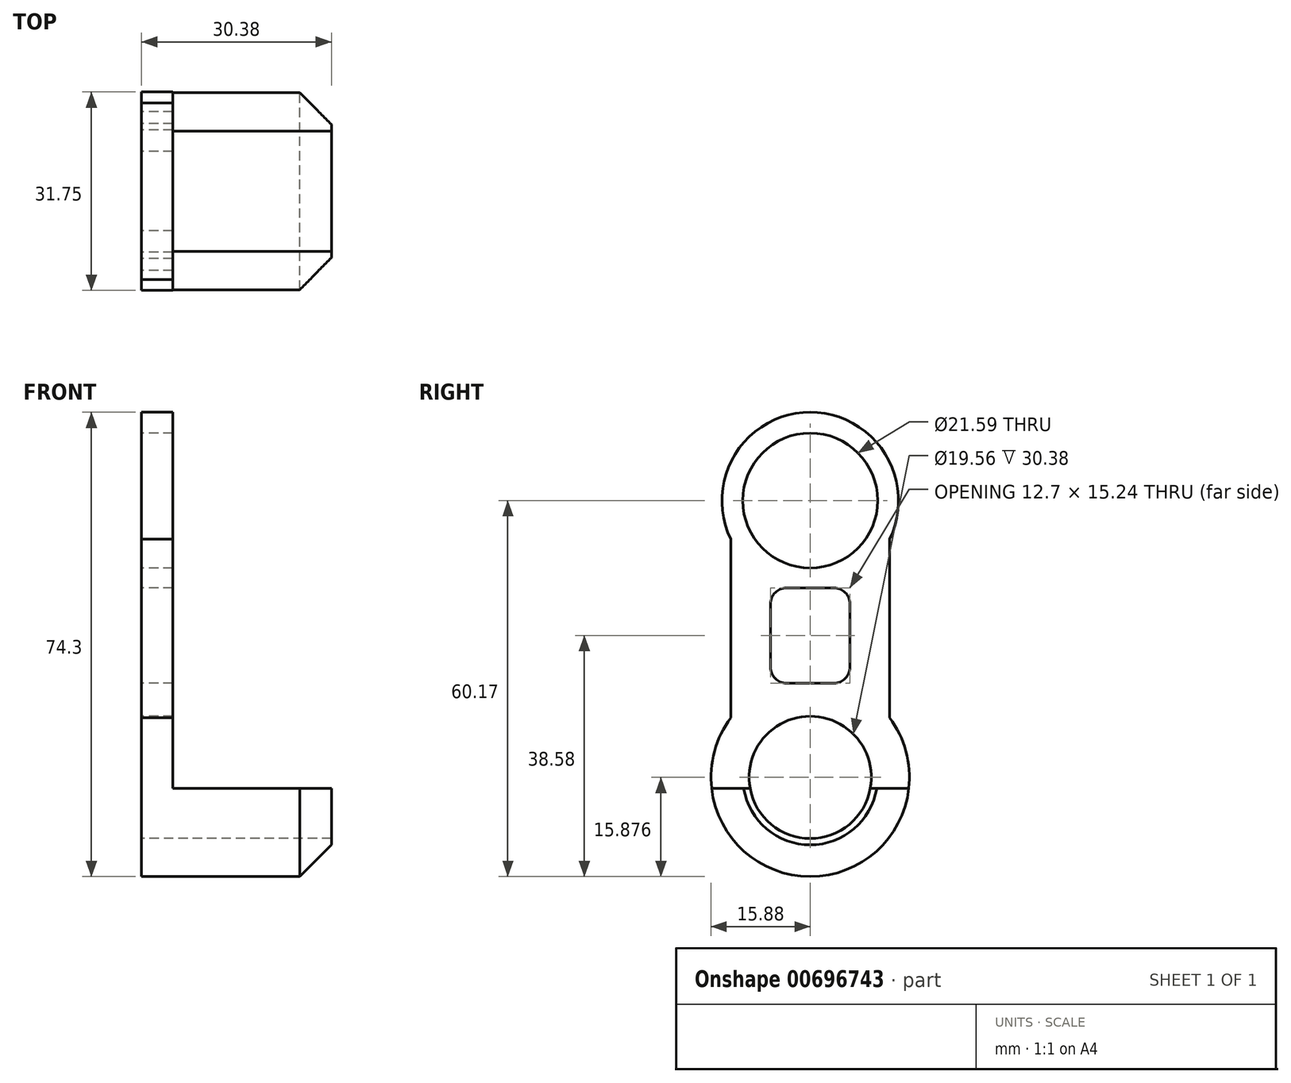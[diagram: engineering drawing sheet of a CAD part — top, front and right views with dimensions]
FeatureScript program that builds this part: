
annotation { "Feature Type Name" : "Feature", "Feature Type Description" : "" }
export const myFeature = defineFeature(function(context is Context, id is Id, definition is map)
    precondition{}
    {
        {
            var Q0;
            Q0=qCreatedBy(makeId("Right.planeOp"),FACE);
            var sketch = newSketch(context, id + "F0", { "sketchPlane" : qUnion([Q0])});
            skCircle(sketch, "E0", {"center": v(0, 0) * mm, "radius": 10.8 * mm});
            skArc(sketch, "E1", {"start": v(12.7, -6.2) * mm, "mid": v(0, 14.13) * mm, "end": v(-12.7, -6.2) * mm});
            skLineSegment(sketch, "E2", {"start": v(-12.7, -6.2) * mm, "end": v(-12.7, -34.77) * mm});
            skLineSegment(sketch, "E3", {"start": v(12.7, -6.2) * mm, "end": v(12.7, -34.77) * mm});
            skCircle(sketch, "E4", {"center": v(0, -44.3) * mm, "radius": 9.78 * mm});
            skArc(sketch, "E5", {"start": v(-12.7, -34.77) * mm, "mid": v(0, -60.17) * mm, "end": v(12.7, -34.77) * mm});
            skLineSegment(sketch, "E6", {"start": v(6.35, -13.97) * mm, "end": v(6.35, -29.21) * mm});
            skLineSegment(sketch, "E7", {"start": v(6.35, -29.21) * mm, "end": v(-6.35, -29.21) * mm});
            skLineSegment(sketch, "E8", {"start": v(-6.35, -29.21) * mm, "end": v(-6.35, -13.97) * mm});
            skLineSegment(sketch, "E9", {"start": v(-6.35, -13.97) * mm, "end": v(6.35, -13.97) * mm});
            skSolve(sketch);
        }
        {
            var Q0;
            Q0=makeQuery(id+"F0.imprint","IMPRINT",FACE,{"disambiguationData":[TD([[makeQuery(id+"F0.imprint","IMPRINT",EDGE,{"derivedFrom":sQuery(id+"F0.wireOp",EDGE,"E0")}),-1.0]])]});
            var Q1;
            {var subQ1=sQuery(id+"F0.wireOp",EDGE,"E2");Q1=makeQuery(id+"F0.imprint","IMPRINT",FACE,{"disambiguationData":[TD([[makeQuery(id+"F0.imprint","IMPRINT",EDGE,{"derivedFrom":subQ1}),1.0]])]});}
            var Q2;
            {var subQ0=sQuery(id+"F0.wireOp",EDGE,"MDCRhlGj-Whgg-Ktwf-GIel-y43xcJZ2J1TR");Q2=makeQuery(id+"F0.imprint","IMPRINT",FACE,{"disambiguationData":[TD([[makeQuery(id+"F0.imprint","IMPRINT",EDGE,{"derivedFrom":subQ0}),-1.0]])]});}
            var Q3;
            Q3=makeQuery(id+"F0.imprint","IMPRINT",FACE,{"disambiguationData":[TD([[makeQuery(id+"F0.imprint","IMPRINT",EDGE,{"derivedFrom":sQuery(id+"F0.wireOp",EDGE,"E4")}),-1.0]])]});
            var Q4;
            {var subQ0=sQuery(id+"F0.wireOp",EDGE,"E5");var subQ1=sQuery(id+"F0.wireOp",EDGE,"5xRPiuOo-jEAR-rATj-yGpN-2LbGpSY4B5gd");var subQ2=makeQuery(id+"F0.imprint","INTERSECT",VERTEX,{"disambiguationData":[OD(0.0)],"derivedFrom":[subQ1,subQ0]});Q4=makeQuery(id+"F0.imprint","IMPRINT",FACE,{"disambiguationData":[TD([[makeQuery(id+"F0.imprint","IMPRINT",EDGE,{"disambiguationData":[TD([[subQ2,-1.0]])],"derivedFrom":subQ1}),1.0]])]});}
            extrude(context, id + "F1", {"entities" : qUnion([Q0, Q1, Q2, Q3, Q4]), "depth" : 4.98 * mm, "offsetDistance" : 25.4 * mm});
        }
        {
            var Q0;
            Q0=makeQuery(id+"F1.opExtrude","CAP_FACE",FACE,{"disambiguationData":[OSD([sQuery(id+"F0.wireOp",EDGE,"E0"),sQuery(id+"F0.wireOp",EDGE,"E1"),sQuery(id+"F0.wireOp",EDGE,"E2"),sQuery(id+"F0.wireOp",EDGE,"E3"),sQuery(id+"F0.wireOp",EDGE,"E4"),sQuery(id+"F0.wireOp",EDGE,"E5")])],"isStart":false});
            var sketch = newSketch(context, id + "F2", { "sketchPlane" : qUnion([Q0])});
            skCircle(sketch, "E10.0", {"center": v(0, -44.3) * mm, "radius": 9.78 * mm});
            skArc(sketch, "E11.0", {"start": v(-12.7, -34.77) * mm, "mid": v(0, -60.17) * mm, "end": v(12.7, -34.77) * mm});
            skLineSegment(sketch, "E12", {"start": v(-9.62, -46.07) * mm, "end": v(-15.78, -46.07) * mm});
            skLineSegment(sketch, "E13", {"start": v(9.62, -46.07) * mm, "end": v(15.78, -46.07) * mm});
            skSolve(sketch);
        }
        {
            var Q0;
            {var subQ0=sQuery(id+"F2.wireOp",EDGE,"E12");Q0=makeQuery(id+"F2.imprint","IMPRINT",FACE,{"disambiguationData":[TD([[makeQuery(id+"F2.imprint","IMPRINT",EDGE,{"derivedFrom":subQ0}),1.0]])]});}
            extrude(context, id + "F3", {"entities" : qUnion([Q0]), "operationType" : NewBodyOperationType.ADD, "depth" : 25.4 * mm, "offsetDistance" : 25.4 * mm});
        }
        {
            var Q0;
            Q0=makeQuery(id+"F3.opExtrude","CAP_EDGE",EDGE,{"disambiguationData":[OSD([sQuery(id+"F2.wireOp",EDGE,"E11.0")])],"isStart":false});
            chamfer(context, id + "F4", {"entities" : qUnion([Q0]), "width" : 5.08 * mm, "tangentPropagation" : true});
        }
        {
            var Q0;
            Q0=makeQuery(id+"F1.opExtrude","SWEPT_EDGE",EDGE,{"disambiguationData":[OSD([sQuery(id+"F0.wireOp",EDGE,"E6"),sQuery(id+"F0.wireOp",EDGE,"E9")])]});
            var Q1;
            Q1=makeQuery(id+"F1.opExtrude","SWEPT_EDGE",EDGE,{"disambiguationData":[OSD([sQuery(id+"F0.wireOp",EDGE,"E8"),sQuery(id+"F0.wireOp",EDGE,"E9")])]});
            var Q2;
            Q2=makeQuery(id+"F1.opExtrude","SWEPT_EDGE",EDGE,{"disambiguationData":[OSD([sQuery(id+"F0.wireOp",EDGE,"E6"),sQuery(id+"F0.wireOp",EDGE,"E7")])]});
            var Q3;
            Q3=makeQuery(id+"F1.opExtrude","SWEPT_EDGE",EDGE,{"disambiguationData":[OSD([sQuery(id+"F0.wireOp",EDGE,"E7"),sQuery(id+"F0.wireOp",EDGE,"E8")])]});
            fillet(context, id + "F5", {"entities" : qUnion([Q0, Q1, Q2, Q3]), "radius" : 2.54 * mm, "tangentPropagation" : true, "allowEdgeOverflow" : false});
        }
    });
